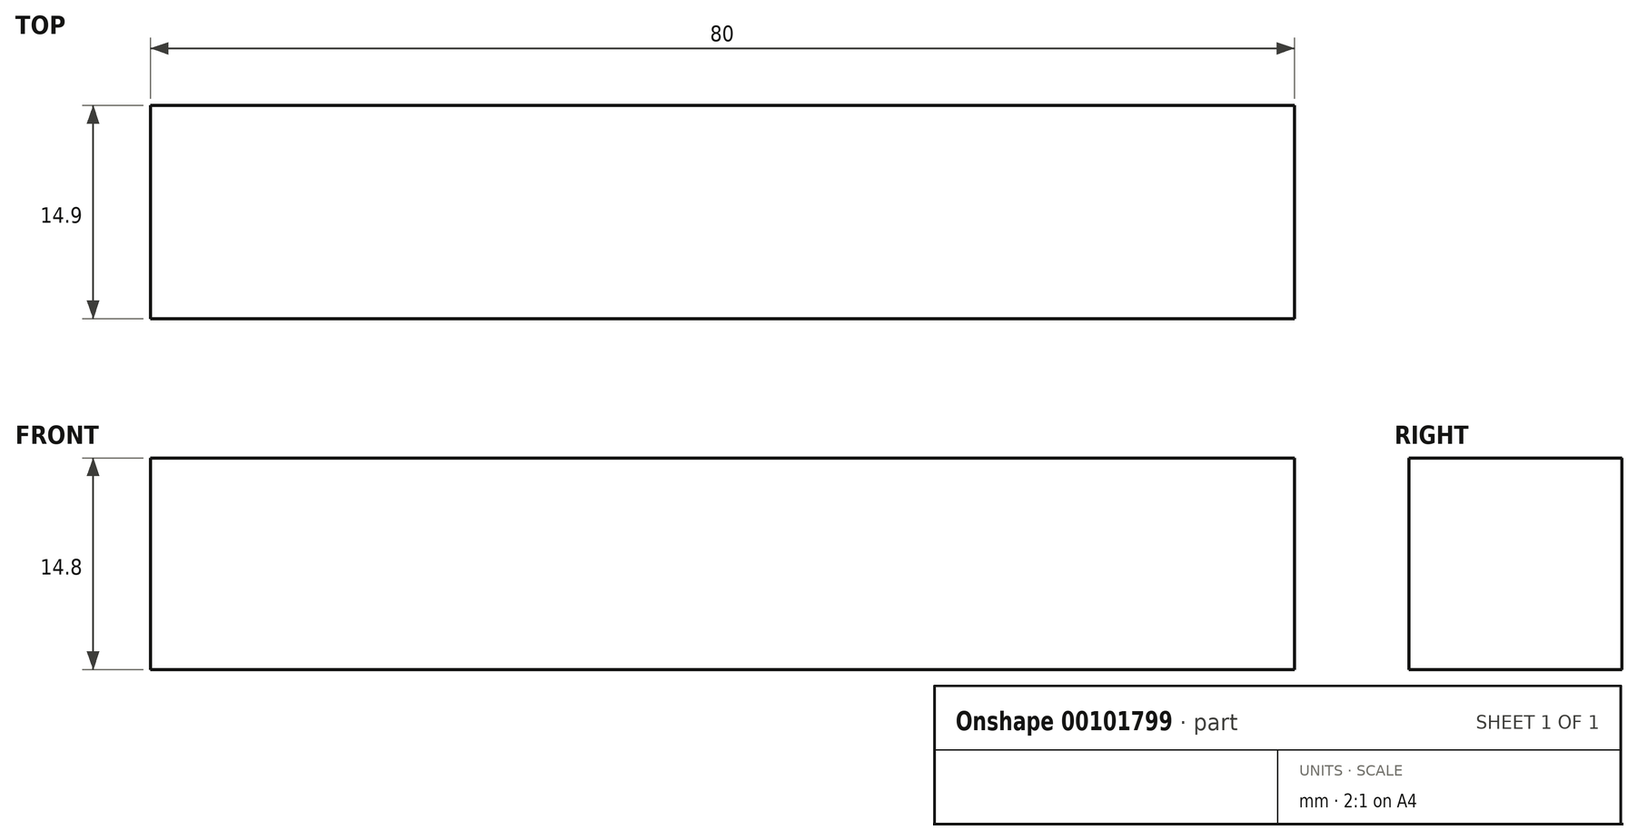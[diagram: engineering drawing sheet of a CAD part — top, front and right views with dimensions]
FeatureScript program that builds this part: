
annotation { "Feature Type Name" : "Feature", "Feature Type Description" : "" }
export const myFeature = defineFeature(function(context is Context, id is Id, definition is map)
    precondition{}
    {
        {
            var Q0;
            Q0=qCreatedBy(makeId("Top.planeOp"),FACE);
            var sketch = newSketch(context, id + "F0", { "sketchPlane" : qUnion([Q0])});
            skLineSegment(sketch, "E0.bottom", {"start": v(40, -7.45) * mm, "end": v(-40, -7.45) * mm});
            skLineSegment(sketch, "E0.top", {"start": v(40, 7.45) * mm, "end": v(-40, 7.45) * mm});
            skLineSegment(sketch, "E0.left", {"start": v(40, -7.45) * mm, "end": v(40, 7.45) * mm});
            skLineSegment(sketch, "E0.right", {"start": v(-40, -7.45) * mm, "end": v(-40, 7.45) * mm});
            skPoint(sketch, "E0.middle", {"position": v(0, 0) * mm});
            skSolve(sketch);
        }
        {
            var Q0;
            Q0=makeQuery(id+"F0.imprint","IMPRINT",FACE,{"disambiguationData":[TD([[makeQuery(id+"F0.imprint","IMPRINT",EDGE,{"derivedFrom":sQuery(id+"F0.wireOp",EDGE,"E0.bottom")}),-1.0]])]});
            extrude(context, id + "F1", {"entities" : qUnion([Q0]), "depth" : 14.8 * mm});
        }
    });
